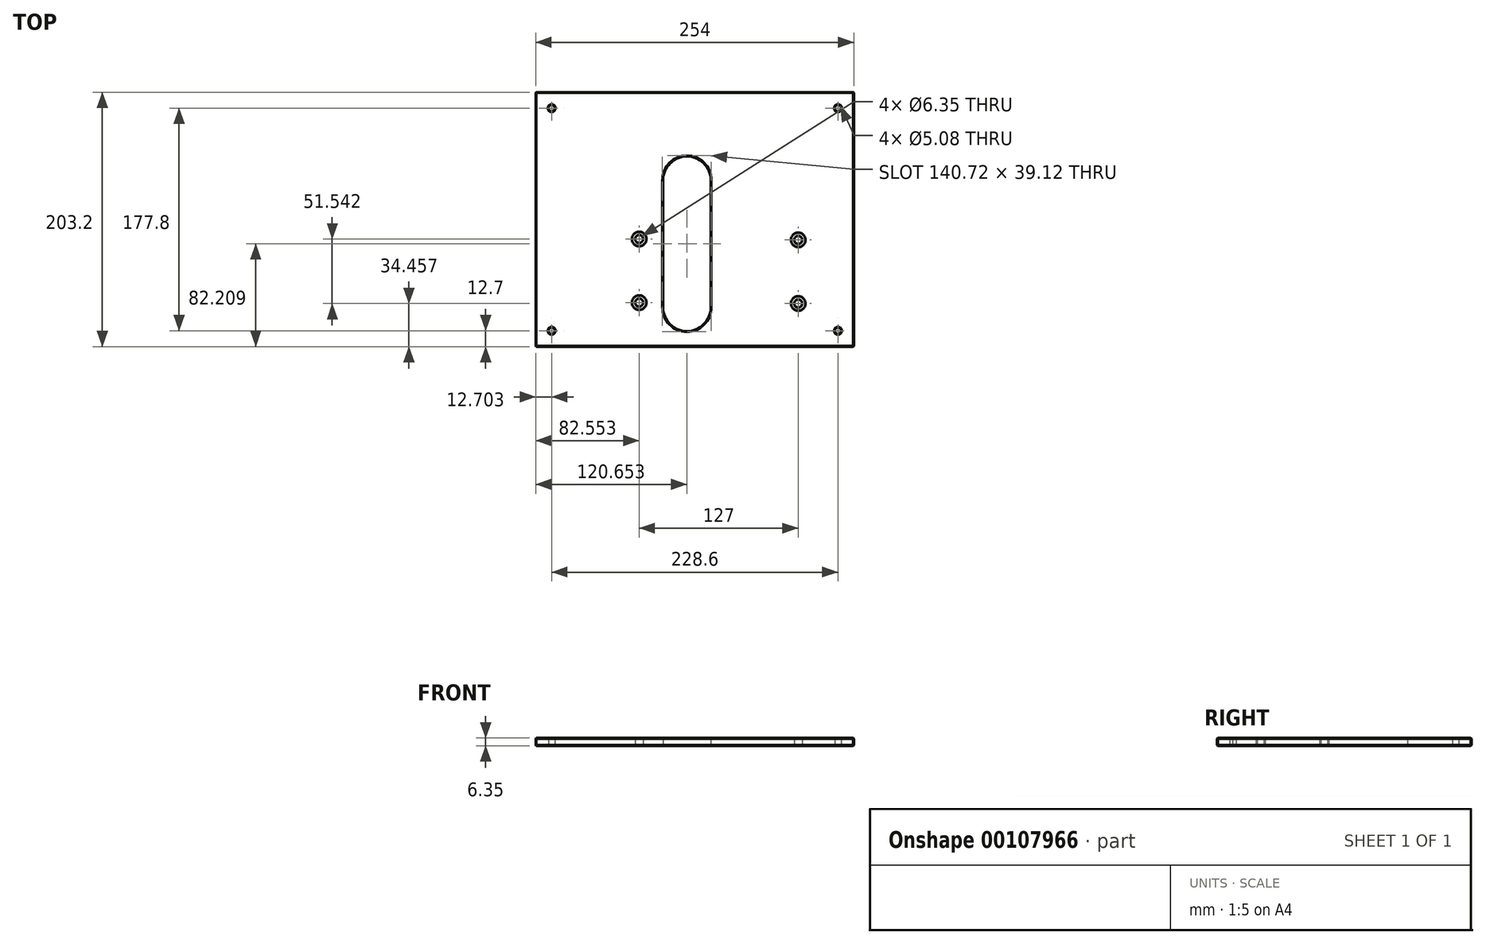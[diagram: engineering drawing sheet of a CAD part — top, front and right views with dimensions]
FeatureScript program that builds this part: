
annotation { "Feature Type Name" : "Feature", "Feature Type Description" : "" }
export const myFeature = defineFeature(function(context is Context, id is Id, definition is map)
    precondition{}
    {
        {
            var Q0;
            Q0=qCreatedBy(makeId("Top.planeOp"),FACE);
            var sketch = newSketch(context, id + "F0", { "sketchPlane" : qUnion([Q0])});
            skLineSegment(sketch, "E0.bottom", {"start": v(141.53, -101.6) * mm, "end": v(-112.47, -101.6) * mm});
            skLineSegment(sketch, "E0.top", {"start": v(141.53, 101.6) * mm, "end": v(-112.47, 101.6) * mm});
            skLineSegment(sketch, "E0.left", {"start": v(141.53, -101.6) * mm, "end": v(141.53, 101.6) * mm});
            skLineSegment(sketch, "E0.right", {"start": v(-112.47, -101.6) * mm, "end": v(-112.47, 101.6) * mm});
            skPoint(sketch, "E0.middle", {"position": v(22.23, -28.05) * mm});
            skCircle(sketch, "E1", {"center": v(97.08, -16.34) * mm, "radius": 3.18 * mm});
            skCircle(sketch, "E2", {"center": v(97.08, -67.14) * mm, "radius": 3.18 * mm});
            skCircle(sketch, "E3", {"center": v(-29.92, -15.6) * mm, "radius": 3.18 * mm});
            skCircle(sketch, "E4", {"center": v(-29.92, -66.4) * mm, "radius": 3.18 * mm});
            skArc(sketch, "E5", {"start": v(-10.87, -70.2) * mm, "mid": v(8.18, -89.24) * mm, "end": v(27.23, -70.2) * mm});
            skArc(sketch, "E6", {"start": v(27.23, 31.4) * mm, "mid": v(8.18, 50.46) * mm, "end": v(-10.87, 31.4) * mm});
            skLineSegment(sketch, "E7", {"start": v(-10.87, 31.4) * mm, "end": v(-10.87, -70.2) * mm});
            skLineSegment(sketch, "E8", {"start": v(27.23, -70.2) * mm, "end": v(27.23, 31.4) * mm});
            skLineSegment(sketch, "E9", {"start": v(-124.21, 88.9) * mm, "end": v(162.26, 88.9) * mm, "construction": true});
            skLineSegment(sketch, "E10", {"start": v(128.83, 120.1) * mm, "end": v(128.83, -124.44) * mm, "construction": true});
            skLineSegment(sketch, "E11", {"start": v(158.6, -88.9) * mm, "end": v(-162.41, -88.9) * mm, "construction": true});
            skLineSegment(sketch, "E12", {"start": v(-99.77, 117.85) * mm, "end": v(-99.77, -118.4) * mm, "construction": true});
            skCircle(sketch, "E13", {"center": v(-99.77, 88.9) * mm, "radius": 2.54 * mm});
            skCircle(sketch, "E14", {"center": v(128.83, 88.9) * mm, "radius": 2.54 * mm});
            skCircle(sketch, "E15", {"center": v(128.83, -88.9) * mm, "radius": 2.54 * mm});
            skCircle(sketch, "E16", {"center": v(-99.77, -88.9) * mm, "radius": 2.54 * mm});
            skSolve(sketch);
        }
        {
            var Q0;
            Q0=makeQuery(id+"F0.imprint","IMPRINT",FACE,{"disambiguationData":[TD([[makeQuery(id+"F0.imprint","IMPRINT",EDGE,{"derivedFrom":sQuery(id+"F0.wireOp",EDGE,"E0.bottom")}),-1.0]])]});
            extrude(context, id + "F1", {"entities" : qUnion([Q0]), "depth" : 6.35 * mm});
        }
        {
            var Q0;
            Q0=makeQuery(id+"F1.opExtrude","CAP_FACE",FACE,{"disambiguationData":[OSD([sQuery(id+"F0.wireOp",EDGE,"E0.bottom"),sQuery(id+"F0.wireOp",EDGE,"E0.top"),sQuery(id+"F0.wireOp",EDGE,"E0.left"),sQuery(id+"F0.wireOp",EDGE,"E0.right"),sQuery(id+"F0.wireOp",EDGE,"E1"),sQuery(id+"F0.wireOp",EDGE,"E2"),sQuery(id+"F0.wireOp",EDGE,"E3"),sQuery(id+"F0.wireOp",EDGE,"E4"),sQuery(id+"F0.wireOp",EDGE,"E5"),sQuery(id+"F0.wireOp",EDGE,"E6"),sQuery(id+"F0.wireOp",EDGE,"E7"),sQuery(id+"F0.wireOp",EDGE,"E8")])],"isStart":false});
            var Q1;
            Q1=makeQuery(id+"F1.opExtrude","CAP_FACE",FACE,{"disambiguationData":[OSD([sQuery(id+"F0.wireOp",EDGE,"E0.bottom"),sQuery(id+"F0.wireOp",EDGE,"E0.top"),sQuery(id+"F0.wireOp",EDGE,"E0.left"),sQuery(id+"F0.wireOp",EDGE,"E0.right"),sQuery(id+"F0.wireOp",EDGE,"E1"),sQuery(id+"F0.wireOp",EDGE,"E2"),sQuery(id+"F0.wireOp",EDGE,"E3"),sQuery(id+"F0.wireOp",EDGE,"E4"),sQuery(id+"F0.wireOp",EDGE,"E5"),sQuery(id+"F0.wireOp",EDGE,"E6"),sQuery(id+"F0.wireOp",EDGE,"E7"),sQuery(id+"F0.wireOp",EDGE,"E8")])],"isStart":true});
            var Q2;
            Q2=makeQuery(id+"F1.opExtrude","SWEPT_EDGE",EDGE,{"disambiguationData":[OSD([sQuery(id+"F0.wireOp",EDGE,"E0.bottom"),sQuery(id+"F0.wireOp",EDGE,"E0.right")])]});
            var Q3;
            Q3=makeQuery(id+"F1.opExtrude","SWEPT_EDGE",EDGE,{"disambiguationData":[OSD([sQuery(id+"F0.wireOp",EDGE,"E0.top"),sQuery(id+"F0.wireOp",EDGE,"E0.right")])]});
            var Q4;
            Q4=makeQuery(id+"F1.opExtrude","SWEPT_EDGE",EDGE,{"disambiguationData":[OSD([sQuery(id+"F0.wireOp",EDGE,"E0.bottom"),sQuery(id+"F0.wireOp",EDGE,"E0.left")])]});
            var Q5;
            Q5=makeQuery(id+"F1.opExtrude","SWEPT_EDGE",EDGE,{"disambiguationData":[OSD([sQuery(id+"F0.wireOp",EDGE,"E0.top"),sQuery(id+"F0.wireOp",EDGE,"E0.left")])]});
            chamfer(context, id + "F2", {"entities" : qUnion([Q0, Q1, Q2, Q3, Q4, Q5]), "width" : 0.5 * mm, "tangentPropagation" : true});
        }
        {
            var Q0;
            {var subQ0=sQuery(id+"F0.wireOp",EDGE,"E4");Q0=makeQuery(id+"F2.opChamfer","BLEND_EDGE",EDGE,{"blendedFrom":[makeQuery(id+"F1.opExtrude","CAP_EDGE",EDGE,{"disambiguationData":[OSD([subQ0])],"isStart":false}),makeQuery(id+"F1.opExtrude","CAP_FACE",FACE,{"disambiguationData":[OSD([sQuery(id+"F0.wireOp",EDGE,"E0.bottom"),sQuery(id+"F0.wireOp",EDGE,"E0.top"),sQuery(id+"F0.wireOp",EDGE,"E0.left"),sQuery(id+"F0.wireOp",EDGE,"E0.right"),sQuery(id+"F0.wireOp",EDGE,"E1"),sQuery(id+"F0.wireOp",EDGE,"E2"),sQuery(id+"F0.wireOp",EDGE,"E3"),subQ0,sQuery(id+"F0.wireOp",EDGE,"E5"),sQuery(id+"F0.wireOp",EDGE,"E6"),sQuery(id+"F0.wireOp",EDGE,"E7"),sQuery(id+"F0.wireOp",EDGE,"E8")])],"isStart":false})],"blendedInto":[makeQuery(id+"F1.opExtrude","CAP_FACE",FACE,{"disambiguationData":[OSD([sQuery(id+"F0.wireOp",EDGE,"E0.bottom"),sQuery(id+"F0.wireOp",EDGE,"E0.top"),sQuery(id+"F0.wireOp",EDGE,"E0.left"),sQuery(id+"F0.wireOp",EDGE,"E0.right"),sQuery(id+"F0.wireOp",EDGE,"E1"),sQuery(id+"F0.wireOp",EDGE,"E2"),sQuery(id+"F0.wireOp",EDGE,"E3"),subQ0,sQuery(id+"F0.wireOp",EDGE,"E5"),sQuery(id+"F0.wireOp",EDGE,"E6"),sQuery(id+"F0.wireOp",EDGE,"E7"),sQuery(id+"F0.wireOp",EDGE,"E8")])],"isStart":false})]});}
            var Q1;
            {var subQ0=sQuery(id+"F0.wireOp",EDGE,"E3");Q1=makeQuery(id+"F2.opChamfer","BLEND_EDGE",EDGE,{"blendedFrom":[makeQuery(id+"F1.opExtrude","CAP_EDGE",EDGE,{"disambiguationData":[OSD([subQ0])],"isStart":false}),makeQuery(id+"F1.opExtrude","CAP_FACE",FACE,{"disambiguationData":[OSD([sQuery(id+"F0.wireOp",EDGE,"E0.bottom"),sQuery(id+"F0.wireOp",EDGE,"E0.top"),sQuery(id+"F0.wireOp",EDGE,"E0.left"),sQuery(id+"F0.wireOp",EDGE,"E0.right"),sQuery(id+"F0.wireOp",EDGE,"E1"),sQuery(id+"F0.wireOp",EDGE,"E2"),subQ0,sQuery(id+"F0.wireOp",EDGE,"E4"),sQuery(id+"F0.wireOp",EDGE,"E5"),sQuery(id+"F0.wireOp",EDGE,"E6"),sQuery(id+"F0.wireOp",EDGE,"E7"),sQuery(id+"F0.wireOp",EDGE,"E8")])],"isStart":false})],"blendedInto":[makeQuery(id+"F1.opExtrude","CAP_FACE",FACE,{"disambiguationData":[OSD([sQuery(id+"F0.wireOp",EDGE,"E0.bottom"),sQuery(id+"F0.wireOp",EDGE,"E0.top"),sQuery(id+"F0.wireOp",EDGE,"E0.left"),sQuery(id+"F0.wireOp",EDGE,"E0.right"),sQuery(id+"F0.wireOp",EDGE,"E1"),sQuery(id+"F0.wireOp",EDGE,"E2"),subQ0,sQuery(id+"F0.wireOp",EDGE,"E4"),sQuery(id+"F0.wireOp",EDGE,"E5"),sQuery(id+"F0.wireOp",EDGE,"E6"),sQuery(id+"F0.wireOp",EDGE,"E7"),sQuery(id+"F0.wireOp",EDGE,"E8")])],"isStart":false})]});}
            var Q2;
            {var subQ0=sQuery(id+"F0.wireOp",EDGE,"E2");Q2=makeQuery(id+"F2.opChamfer","BLEND_EDGE",EDGE,{"blendedFrom":[makeQuery(id+"F1.opExtrude","CAP_EDGE",EDGE,{"disambiguationData":[OSD([subQ0])],"isStart":false}),makeQuery(id+"F1.opExtrude","CAP_FACE",FACE,{"disambiguationData":[OSD([sQuery(id+"F0.wireOp",EDGE,"E0.bottom"),sQuery(id+"F0.wireOp",EDGE,"E0.top"),sQuery(id+"F0.wireOp",EDGE,"E0.left"),sQuery(id+"F0.wireOp",EDGE,"E0.right"),sQuery(id+"F0.wireOp",EDGE,"E1"),subQ0,sQuery(id+"F0.wireOp",EDGE,"E3"),sQuery(id+"F0.wireOp",EDGE,"E4"),sQuery(id+"F0.wireOp",EDGE,"E5"),sQuery(id+"F0.wireOp",EDGE,"E6"),sQuery(id+"F0.wireOp",EDGE,"E7"),sQuery(id+"F0.wireOp",EDGE,"E8")])],"isStart":false})],"blendedInto":[makeQuery(id+"F1.opExtrude","CAP_FACE",FACE,{"disambiguationData":[OSD([sQuery(id+"F0.wireOp",EDGE,"E0.bottom"),sQuery(id+"F0.wireOp",EDGE,"E0.top"),sQuery(id+"F0.wireOp",EDGE,"E0.left"),sQuery(id+"F0.wireOp",EDGE,"E0.right"),sQuery(id+"F0.wireOp",EDGE,"E1"),subQ0,sQuery(id+"F0.wireOp",EDGE,"E3"),sQuery(id+"F0.wireOp",EDGE,"E4"),sQuery(id+"F0.wireOp",EDGE,"E5"),sQuery(id+"F0.wireOp",EDGE,"E6"),sQuery(id+"F0.wireOp",EDGE,"E7"),sQuery(id+"F0.wireOp",EDGE,"E8")])],"isStart":false})]});}
            var Q3;
            {var subQ0=sQuery(id+"F0.wireOp",EDGE,"E1");Q3=makeQuery(id+"F2.opChamfer","BLEND_EDGE",EDGE,{"blendedFrom":[makeQuery(id+"F1.opExtrude","CAP_EDGE",EDGE,{"disambiguationData":[OSD([subQ0])],"isStart":false}),makeQuery(id+"F1.opExtrude","CAP_FACE",FACE,{"disambiguationData":[OSD([sQuery(id+"F0.wireOp",EDGE,"E0.bottom"),sQuery(id+"F0.wireOp",EDGE,"E0.top"),sQuery(id+"F0.wireOp",EDGE,"E0.left"),sQuery(id+"F0.wireOp",EDGE,"E0.right"),subQ0,sQuery(id+"F0.wireOp",EDGE,"E2"),sQuery(id+"F0.wireOp",EDGE,"E3"),sQuery(id+"F0.wireOp",EDGE,"E4"),sQuery(id+"F0.wireOp",EDGE,"E5"),sQuery(id+"F0.wireOp",EDGE,"E6"),sQuery(id+"F0.wireOp",EDGE,"E7"),sQuery(id+"F0.wireOp",EDGE,"E8")])],"isStart":false})],"blendedInto":[makeQuery(id+"F1.opExtrude","CAP_FACE",FACE,{"disambiguationData":[OSD([sQuery(id+"F0.wireOp",EDGE,"E0.bottom"),sQuery(id+"F0.wireOp",EDGE,"E0.top"),sQuery(id+"F0.wireOp",EDGE,"E0.left"),sQuery(id+"F0.wireOp",EDGE,"E0.right"),subQ0,sQuery(id+"F0.wireOp",EDGE,"E2"),sQuery(id+"F0.wireOp",EDGE,"E3"),sQuery(id+"F0.wireOp",EDGE,"E4"),sQuery(id+"F0.wireOp",EDGE,"E5"),sQuery(id+"F0.wireOp",EDGE,"E6"),sQuery(id+"F0.wireOp",EDGE,"E7"),sQuery(id+"F0.wireOp",EDGE,"E8")])],"isStart":false})]});}
            chamfer(context, id + "F3", {"entities" : qUnion([Q0, Q1, Q2, Q3]), "width" : 5.08 * mm, "tangentPropagation" : true});
        }
    });
